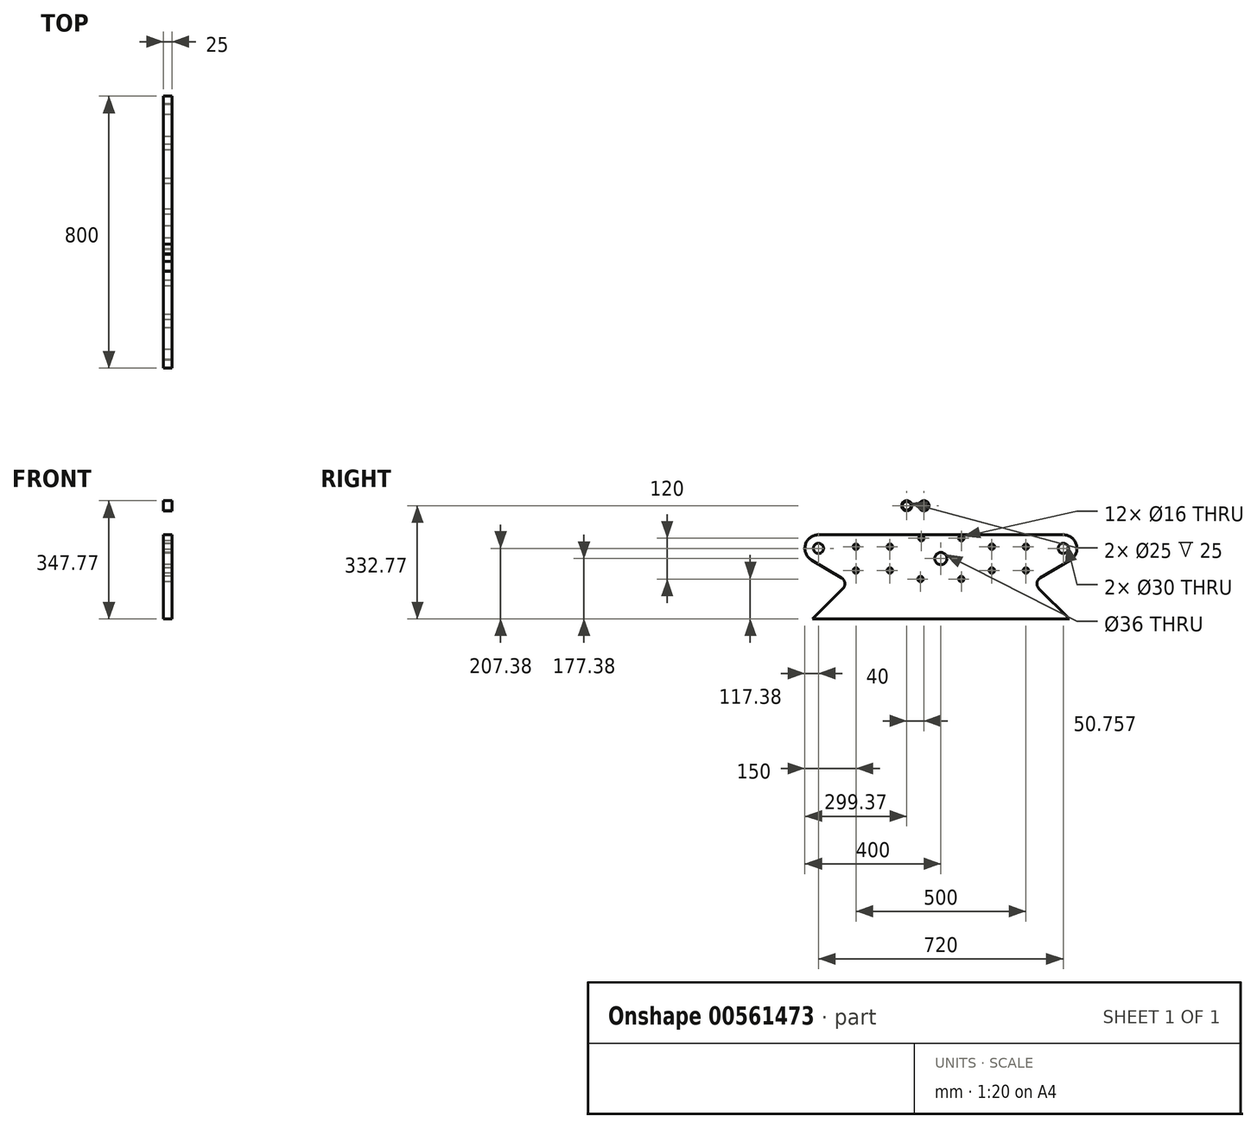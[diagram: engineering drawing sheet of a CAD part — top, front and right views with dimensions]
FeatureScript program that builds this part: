
annotation { "Feature Type Name" : "Feature", "Feature Type Description" : "" }
export const myFeature = defineFeature(function(context is Context, id is Id, definition is map)
    precondition{}
    {
        {
            var Q0;
            Q0=qCreatedBy(makeId("Right.planeOp"),FACE);
            var sketch = newSketch(context, id + "F0", { "sketchPlane" : qUnion([Q0])});
            skLineSegment(sketch, "E0.bottom", {"start": v(-270, 70) * mm, "end": v(270, 70) * mm});
            skLineSegment(sketch, "E0.top", {"start": v(-270, -70) * mm, "end": v(270, -70) * mm});
            skLineSegment(sketch, "E0.left", {"start": v(-270, 70) * mm, "end": v(-270, -70) * mm});
            skLineSegment(sketch, "E0.right", {"start": v(270, 70) * mm, "end": v(270, -70) * mm});
            skCircle(sketch, "E1", {"center": v(-250, 35) * mm, "radius": 8 * mm});
            skCircle(sketch, "E2", {"center": v(-150, 35) * mm, "radius": 8 * mm});
            skCircle(sketch, "E3", {"center": v(-250, -35) * mm, "radius": 8 * mm});
            skCircle(sketch, "E4", {"center": v(-150, -35) * mm, "radius": 8 * mm});
            skCircle(sketch, "E5", {"center": v(150, 35) * mm, "radius": 8 * mm});
            skCircle(sketch, "E6", {"center": v(250, 35) * mm, "radius": 8 * mm});
            skCircle(sketch, "E7", {"center": v(150, -35) * mm, "radius": 8 * mm});
            skCircle(sketch, "E8", {"center": v(250, -35) * mm, "radius": 8 * mm});
            skCircle(sketch, "E9", {"center": v(0, 0) * mm, "radius": 18 * mm});
            skCircle(sketch, "E10", {"center": v(-360, 30) * mm, "radius": 40 * mm});
            skCircle(sketch, "E11", {"center": v(-360, 30) * mm, "radius": 15 * mm});
            skCircle(sketch, "E12", {"center": v(360, 30) * mm, "radius": 15 * mm});
            skCircle(sketch, "E13", {"center": v(360, 30) * mm, "radius": 40 * mm});
            skLineSegment(sketch, "E14", {"start": v(-270, 70) * mm, "end": v(-360, 70) * mm});
            skLineSegment(sketch, "E15", {"start": v(-270, -70) * mm, "end": v(-380.43, -4.39) * mm});
            skLineSegment(sketch, "E16", {"start": v(270, 70) * mm, "end": v(360, 70) * mm});
            skLineSegment(sketch, "E17", {"start": v(270, -70) * mm, "end": v(380.43, -4.39) * mm});
            skCircle(sketch, "E18", {"center": v(-60, -60) * mm, "radius": 8 * mm});
            skCircle(sketch, "E19", {"center": v(60, 60) * mm, "radius": 8 * mm});
            skCircle(sketch, "E20", {"center": v(-57.3, 60) * mm, "radius": 8 * mm});
            skCircle(sketch, "E21", {"center": v(60, -60) * mm, "radius": 8 * mm});
            skLineSegment(sketch, "E22", {"start": v(-270, -70) * mm, "end": v(-377.38, -177.38) * mm});
            skLineSegment(sketch, "E23", {"start": v(-377.38, -177.38) * mm, "end": v(377.38, -177.38) * mm});
            skLineSegment(sketch, "E24", {"start": v(377.38, -177.38) * mm, "end": v(270, -70) * mm});
            skSolve(sketch);
        }
        {
            var Q0;
            Q0=makeQuery(id+"F0.imprint","IMPRINT",FACE,{"disambiguationData":[TD([[makeQuery(id+"F0.imprint","IMPRINT",EDGE,{"derivedFrom":sQuery(id+"F0.wireOp",EDGE,"E0.bottom")}),-1.0]])]});
            var Q1;
            Q1=makeQuery(id+"F0.imprint","IMPRINT",FACE,{"disambiguationData":[TD([[makeQuery(id+"F0.imprint","IMPRINT",EDGE,{"derivedFrom":sQuery(id+"F0.wireOp",EDGE,"E0.left")}),-1.0]])]});
            var Q2;
            Q2=makeQuery(id+"F0.imprint","IMPRINT",FACE,{"disambiguationData":[TD([[makeQuery(id+"F0.imprint","IMPRINT",EDGE,{"derivedFrom":sQuery(id+"F0.wireOp",EDGE,"8rtlSDpM-EiBH-vkZ4-tMwM-JQEAZcyMxOtp")}),-1.0]])]});
            var Q3;
            Q3=makeQuery(id+"F0.imprint","IMPRINT",FACE,{"disambiguationData":[TD([[makeQuery(id+"F0.imprint","IMPRINT",EDGE,{"derivedFrom":sQuery(id+"F0.wireOp",EDGE,"E0.right")}),1.0]])]});
            var Q4;
            Q4=makeQuery(id+"F0.imprint","IMPRINT",FACE,{"disambiguationData":[TD([[makeQuery(id+"F0.imprint","IMPRINT",EDGE,{"derivedFrom":sQuery(id+"F0.wireOp",EDGE,"nt3cSNqV-kbGH-THf3-3oYD-Qz9JgZJjk8rZ")}),-1.0]])]});
            var Q5;
            Q5=makeQuery(id+"F0.imprint","IMPRINT",FACE,{"disambiguationData":[TD([[makeQuery(id+"F0.imprint","IMPRINT",EDGE,{"derivedFrom":sQuery(id+"F0.wireOp",EDGE,"E11")}),-1.0]])]});
            var Q6;
            Q6=makeQuery(id+"F0.imprint","IMPRINT",FACE,{"disambiguationData":[TD([[makeQuery(id+"F0.imprint","IMPRINT",EDGE,{"derivedFrom":sQuery(id+"F0.wireOp",EDGE,"E12")}),-1.0]])]});
            var Q7;
            Q7=makeQuery(id+"F0.imprint","IMPRINT",FACE,{"disambiguationData":[TD([[makeQuery(id+"F0.imprint","IMPRINT",EDGE,{"derivedFrom":sQuery(id+"F0.wireOp",EDGE,"E0.top")}),-1.0]])]});
            extrude(context, id + "F1", {"entities" : qUnion([Q0, Q1, Q2, Q3, Q4, Q5, Q6, Q7]), "depth" : 25 * mm, "offsetDistance" : 25 * mm});
        }
        {
            var Q0;
            Q0=qCreatedBy(makeId("Right.planeOp"),FACE);
            var sketch = newSketch(context, id + "F2", { "sketchPlane" : qUnion([Q0])});
            skCircle(sketch, "E25", {"center": v(-213.56, 155.4) * mm, "radius": 15 * mm});
            skCircle(sketch, "E26", {"center": v(-213.56, 155.4) * mm, "radius": 12.5 * mm});
            skCircle(sketch, "E27", {"center": v(-154.94, 155.4) * mm, "radius": 15 * mm});
            skCircle(sketch, "E28", {"center": v(-154.94, 155.4) * mm, "radius": 12.5 * mm});
            skCircle(sketch, "E29", {"center": v(-100.63, 155.4) * mm, "radius": 12.5 * mm});
            skCircle(sketch, "E30", {"center": v(-100.63, 155.4) * mm, "radius": 15 * mm});
            skCircle(sketch, "E31", {"center": v(-49.87, 155.4) * mm, "radius": 15 * mm});
            skCircle(sketch, "E32", {"center": v(-49.87, 155.4) * mm, "radius": 12.5 * mm});
            skSolve(sketch);
        }
        {
            var Q0;
            Q0=makeQuery(id+"F2.imprint","IMPRINT",FACE,{"disambiguationData":[TD([[makeQuery(id+"F2.imprint","IMPRINT",EDGE,{"derivedFrom":sQuery(id+"F2.wireOp",EDGE,"E25")}),1.0]])]});
            var Q1;
            Q1=makeQuery(id+"F2.imprint","IMPRINT",FACE,{"disambiguationData":[TD([[makeQuery(id+"F2.imprint","IMPRINT",EDGE,{"derivedFrom":sQuery(id+"F2.wireOp",EDGE,"E27")}),1.0]])]});
            var Q2;
            Q2=makeQuery(id+"F2.imprint","IMPRINT",FACE,{"disambiguationData":[TD([[makeQuery(id+"F2.imprint","IMPRINT",EDGE,{"derivedFrom":sQuery(id+"F2.wireOp",EDGE,"E29")}),-1.0]])]});
            var Q3;
            Q3=makeQuery(id+"F2.imprint","IMPRINT",FACE,{"disambiguationData":[TD([[makeQuery(id+"F2.imprint","IMPRINT",EDGE,{"derivedFrom":sQuery(id+"F2.wireOp",EDGE,"E31")}),1.0]])]});
            extrude(context, id + "F3", {"entities" : qUnion([Q0, Q1, Q2, Q3]), "depth" : 25 * mm, "offsetDistance" : 25 * mm});
        }
        {
            var Q0;
            Q0=makeQuery(id+"F3.opExtrude","SWEPT_BODY",BODY,{"disambiguationData":[OSD([sQuery(id+"F2.wireOp",EDGE,"E27"),sQuery(id+"F2.wireOp",EDGE,"E28")])]});
            deleteBodies(context, id + "F4", {"entities" : qUnion([Q0])});
        }
        {
            var Q0;
            Q0=makeQuery(id+"F3.opExtrude","SWEPT_BODY",BODY,{"disambiguationData":[OSD([sQuery(id+"F2.wireOp",EDGE,"E25"),sQuery(id+"F2.wireOp",EDGE,"E26")])]});
            deleteBodies(context, id + "F5", {"entities" : qUnion([Q0])});
        }
        {
            var Q0;
            Q0=makeQuery(id+"F1.opExtrude","SWEPT_EDGE",EDGE,{"disambiguationData":[OSD([sQuery(id+"F0.wireOp",EDGE,"E0.top"),sQuery(id+"F0.wireOp",EDGE,"E0.left"),sQuery(id+"F0.wireOp",EDGE,"E15"),sQuery(id+"F0.wireOp",EDGE,"E22")])]});
            var Q1;
            Q1=makeQuery(id+"F1.opExtrude","SWEPT_EDGE",EDGE,{"disambiguationData":[OSD([sQuery(id+"F0.wireOp",EDGE,"E0.top"),sQuery(id+"F0.wireOp",EDGE,"E0.right"),sQuery(id+"F0.wireOp",EDGE,"E17"),sQuery(id+"F0.wireOp",EDGE,"E24")])]});
            fillet(context, id + "F6", {"entities" : qUnion([Q0, Q1]), "radius" : 20 * mm, "tangentPropagation" : true, "allowEdgeOverflow" : false});
        }
    });
